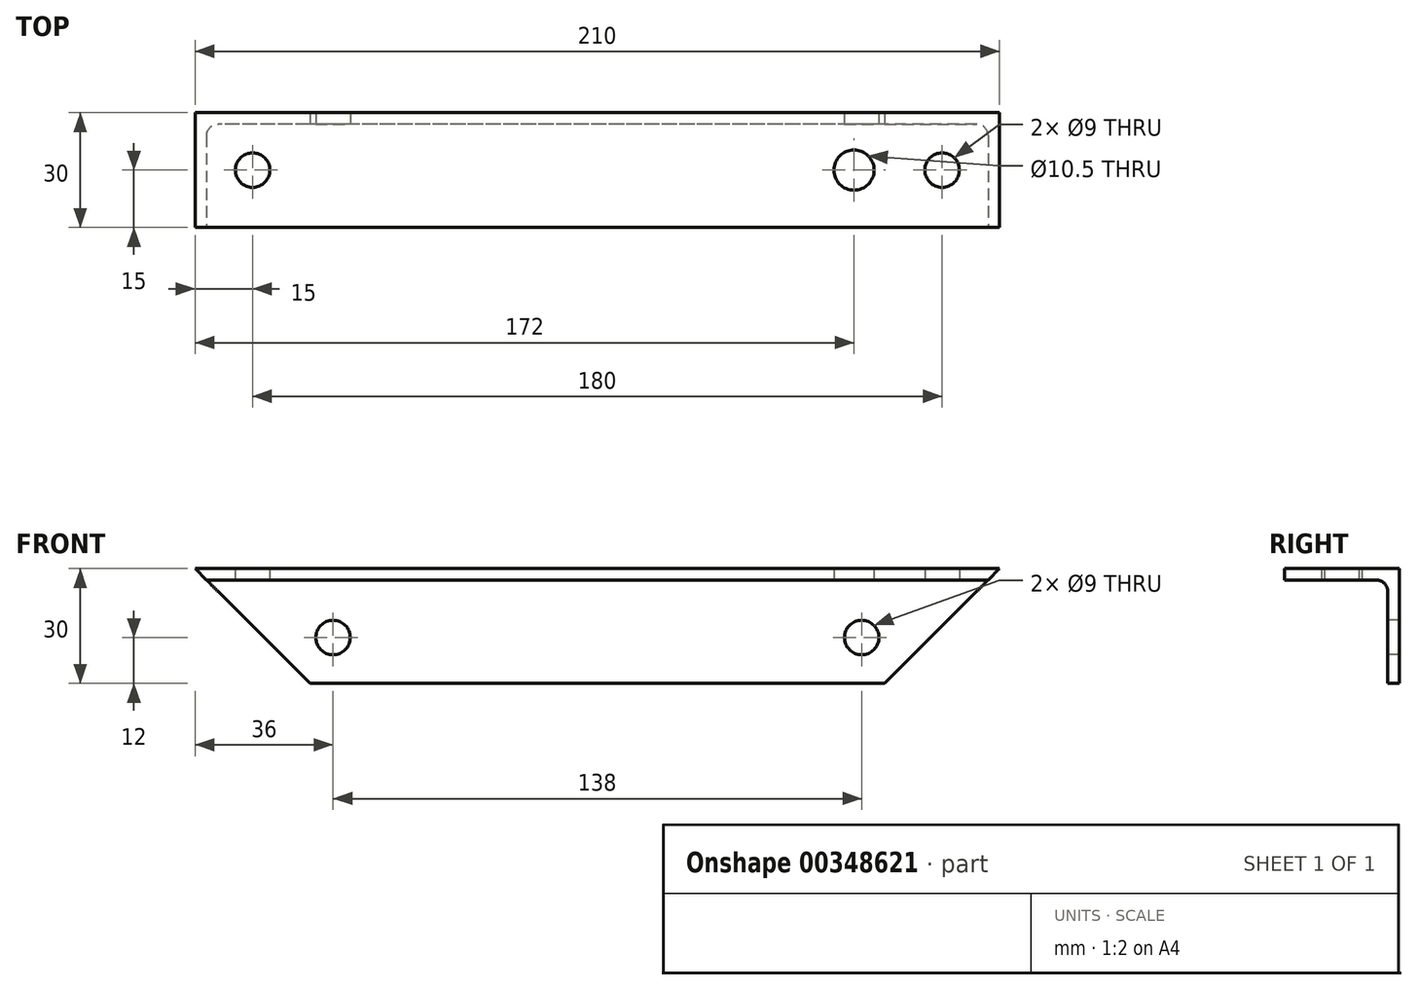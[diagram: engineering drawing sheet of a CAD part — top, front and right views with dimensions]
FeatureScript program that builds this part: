
annotation { "Feature Type Name" : "Feature", "Feature Type Description" : "" }
export const myFeature = defineFeature(function(context is Context, id is Id, definition is map)
    precondition{}
    {
        {
            var Q0;
            Q0=qCreatedBy(makeId("Right.planeOp"),FACE);
            var sketch = newSketch(context, id + "F0", { "sketchPlane" : qUnion([Q0])});
            skLineSegment(sketch, "E0", {"start": v(0, 0) * mm, "end": v(0, 30) * mm});
            skLineSegment(sketch, "E1", {"start": v(0, 30) * mm, "end": v(-30, 30) * mm});
            skLineSegment(sketch, "E2", {"start": v(-30, 30) * mm, "end": v(-30, 27) * mm});
            skLineSegment(sketch, "E3", {"start": v(-30, 27) * mm, "end": v(-6, 27) * mm});
            skLineSegment(sketch, "E4", {"start": v(-3, 24) * mm, "end": v(-3, 0) * mm});
            skLineSegment(sketch, "E5", {"start": v(-3, 0) * mm, "end": v(0, 0) * mm});
            skPoint(sketch, "E6.visualSharp", {"position": v(-3, 27) * mm});
            skArc(sketch, "E6.filletArc", {"start": v(-3, 24) * mm, "mid": v(-3.88, 26.12) * mm, "end": v(-6, 27) * mm});
            skSolve(sketch);
        }
        {
            var Q0;
            Q0=makeQuery(id+"F0.imprint","IMPRINT",FACE,{"disambiguationData":[TD([[makeQuery(id+"F0.imprint","IMPRINT",EDGE,{"derivedFrom":sQuery(id+"F0.wireOp",EDGE,"E0")}),1.0]])]});
            extrude(context, id + "F1", {"entities" : qUnion([Q0]), "depth" : 210 * mm});
        }
        {
            var Q0;
            Q0=makeQuery(id+"F1.opExtrude","SWEPT_FACE",FACE,{"disambiguationData":[OSD([sQuery(id+"F0.wireOp",EDGE,"E4")])]});
            var sketch = newSketch(context, id + "F2", { "sketchPlane" : qUnion([Q0])});
            skPoint(sketch, "E7", {"position": v(36, 12) * mm});
            skPoint(sketch, "E8", {"position": v(174, 12) * mm});
            skSolve(sketch);
        }
        {
            var Q0;
            Q0=sQuery(id+"F2.wireOp",VERTEX,"E7");
            var Q1;
            Q1=sQuery(id+"F2.wireOp",VERTEX,"E8");
            var Q2;
            Q2=makeQuery(id+"F1.opExtrude","SWEPT_BODY",BODY,{"disambiguationData":[OSD([sQuery(id+"F0.wireOp",EDGE,"E0"),sQuery(id+"F0.wireOp",EDGE,"E1"),sQuery(id+"F0.wireOp",EDGE,"E2"),sQuery(id+"F0.wireOp",EDGE,"E3"),sQuery(id+"F0.wireOp",EDGE,"E4"),sQuery(id+"F0.wireOp",EDGE,"E5"),sQuery(id+"F0.wireOp",EDGE,"E6.filletArc")])]});
            hole(context, id + "F3", {"style" : HoleStyle.SIMPLE, "endStyle" : HoleEndStyle.BLIND, "holeDiameter" : 9 * mm, "holeDepth" : 12 * mm, "isTappedThrough" : true, "tappedDepth" : 12 * mm, "tapClearance" : 3, "locations" : qUnion([Q0, Q1]), "scope" : qUnion([Q2])});
        }
        {
            var Q0;
            Q0=makeQuery(id+"F1.opExtrude","SWEPT_FACE",FACE,{"disambiguationData":[OSD([sQuery(id+"F0.wireOp",EDGE,"E2")])]});
            var sketch = newSketch(context, id + "F4", { "sketchPlane" : qUnion([Q0])});
            skLineSegment(sketch, "E9", {"start": v(0, 30) * mm, "end": v(30, 0) * mm});
            skLineSegment(sketch, "E10", {"start": v(30, 0) * mm, "end": v(0, 0) * mm});
            skLineSegment(sketch, "E11", {"start": v(0, 0) * mm, "end": v(0, 30) * mm});
            skLineSegment(sketch, "E12", {"start": v(210, 30) * mm, "end": v(180, 0) * mm});
            skLineSegment(sketch, "E13", {"start": v(180, 0) * mm, "end": v(210, 0) * mm});
            skLineSegment(sketch, "E14", {"start": v(210, 0) * mm, "end": v(210, 30) * mm});
            skSolve(sketch);
        }
        {
            var Q0;
            {var subQ0=sQuery(id+"F4.wireOp",EDGE,"E10");Q0=makeQuery(id+"F4.imprint","IMPRINT",FACE,{"disambiguationData":[TD([[makeQuery(id+"F4.imprint","IMPRINT",EDGE,{"derivedFrom":subQ0}),-1.0]])]});}
            var Q1;
            {var subQ1=sQuery(id+"F4.wireOp",EDGE,"E9");var subQ2=sQuery(id+"F0.wireOp",EDGE,"E2");var subQ4=makeQuery(id+"F1.opExtrude","SWEPT_EDGE",EDGE,{"disambiguationData":[OSD([subQ2,sQuery(id+"F0.wireOp",EDGE,"E3")])]});var subQ5=makeQuery(id+"F4.imprint","INTERSECT",VERTEX,{"derivedFrom":[subQ4,subQ1]});Q1=makeQuery(id+"F4.imprint","IMPRINT",FACE,{"disambiguationData":[TD([[makeQuery(id+"F4.imprint","IMPRINT",EDGE,{"disambiguationData":[TD([[subQ5,1.0]])],"derivedFrom":subQ1}),-1.0]])]});}
            var Q2;
            {var subQ1=sQuery(id+"F4.wireOp",EDGE,"E12");var subQ2=sQuery(id+"F0.wireOp",EDGE,"E2");var subQ4=makeQuery(id+"F1.opExtrude","SWEPT_EDGE",EDGE,{"disambiguationData":[OSD([subQ2,sQuery(id+"F0.wireOp",EDGE,"E3")])]});var subQ5=makeQuery(id+"F4.imprint","INTERSECT",VERTEX,{"derivedFrom":[subQ4,subQ1]});Q2=makeQuery(id+"F4.imprint","IMPRINT",FACE,{"disambiguationData":[TD([[makeQuery(id+"F4.imprint","IMPRINT",EDGE,{"disambiguationData":[TD([[subQ5,1.0]])],"derivedFrom":subQ1}),1.0]])]});}
            var Q3;
            {var subQ0=sQuery(id+"F4.wireOp",EDGE,"E13");Q3=makeQuery(id+"F4.imprint","IMPRINT",FACE,{"disambiguationData":[TD([[makeQuery(id+"F4.imprint","IMPRINT",EDGE,{"derivedFrom":subQ0}),1.0]])]});}
            extrude(context, id + "F5", {"entities" : qUnion([Q0, Q1, Q2, Q3]), "operationType" : NewBodyOperationType.REMOVE, "oppositeDirection" : true, "depth" : 95 * mm});
        }
        {
            var Q0;
            Q0=makeQuery(id+"F1.opExtrude","SWEPT_FACE",FACE,{"disambiguationData":[OSD([sQuery(id+"F0.wireOp",EDGE,"E3")])]});
            var sketch = newSketch(context, id + "F6", { "sketchPlane" : qUnion([Q0])});
            skPoint(sketch, "E15", {"position": v(15, 15) * mm});
            skPoint(sketch, "E16", {"position": v(195, 15) * mm});
            skLineSegment(sketch, "E17", {"start": v(105, 30) * mm, "end": v(105, 0) * mm, "construction": true});
            skSolve(sketch);
        }
        {
            var Q0;
            Q0=sQuery(id+"F6.wireOp",VERTEX,"E15");
            var Q1;
            Q1=sQuery(id+"F6.wireOp",VERTEX,"E16");
            var Q2;
            Q2=makeQuery(id+"F1.opExtrude","SWEPT_BODY",BODY,{"disambiguationData":[OSD([sQuery(id+"F0.wireOp",EDGE,"E0"),sQuery(id+"F0.wireOp",EDGE,"E1"),sQuery(id+"F0.wireOp",EDGE,"E2"),sQuery(id+"F0.wireOp",EDGE,"E3"),sQuery(id+"F0.wireOp",EDGE,"E4"),sQuery(id+"F0.wireOp",EDGE,"E5"),sQuery(id+"F0.wireOp",EDGE,"E6.filletArc")])]});
            hole(context, id + "F7", {"style" : HoleStyle.SIMPLE, "endStyle" : HoleEndStyle.BLIND, "holeDiameter" : 9 * mm, "holeDepth" : 12 * mm, "isTappedThrough" : true, "tappedDepth" : 12 * mm, "tapClearance" : 3, "locations" : qUnion([Q0, Q1]), "scope" : qUnion([Q2])});
        }
        {
            var Q0;
            Q0=makeQuery(id+"F1.opExtrude","SWEPT_FACE",FACE,{"disambiguationData":[OSD([sQuery(id+"F0.wireOp",EDGE,"E3")])]});
            var sketch = newSketch(context, id + "F8", { "sketchPlane" : qUnion([Q0])});
            skPoint(sketch, "E18", {"position": v(172, 15) * mm});
            skLineSegment(sketch, "E19", {"start": v(195, 15) * mm, "end": v(172, 15) * mm, "construction": true});
            skLineSegment(sketch, "E20", {"start": v(105, 30) * mm, "end": v(105, 0) * mm, "construction": true});
            skSolve(sketch);
        }
        {
            var Q0;
            Q0=sQuery(id+"F8.wireOp",VERTEX,"E18");
            var Q1;
            Q1=makeQuery(id+"F1.opExtrude","SWEPT_BODY",BODY,{"disambiguationData":[OSD([sQuery(id+"F0.wireOp",EDGE,"E0"),sQuery(id+"F0.wireOp",EDGE,"E1"),sQuery(id+"F0.wireOp",EDGE,"E2"),sQuery(id+"F0.wireOp",EDGE,"E3"),sQuery(id+"F0.wireOp",EDGE,"E4"),sQuery(id+"F0.wireOp",EDGE,"E5"),sQuery(id+"F0.wireOp",EDGE,"E6.filletArc")])]});
            hole(context, id + "F9", {"style" : HoleStyle.SIMPLE, "endStyle" : HoleEndStyle.BLIND, "holeDiameter" : 10.5 * mm, "holeDepth" : 12 * mm, "isTappedThrough" : true, "tappedDepth" : 12 * mm, "tapClearance" : 3, "locations" : qUnion([Q0]), "scope" : qUnion([Q1])});
        }
    });
